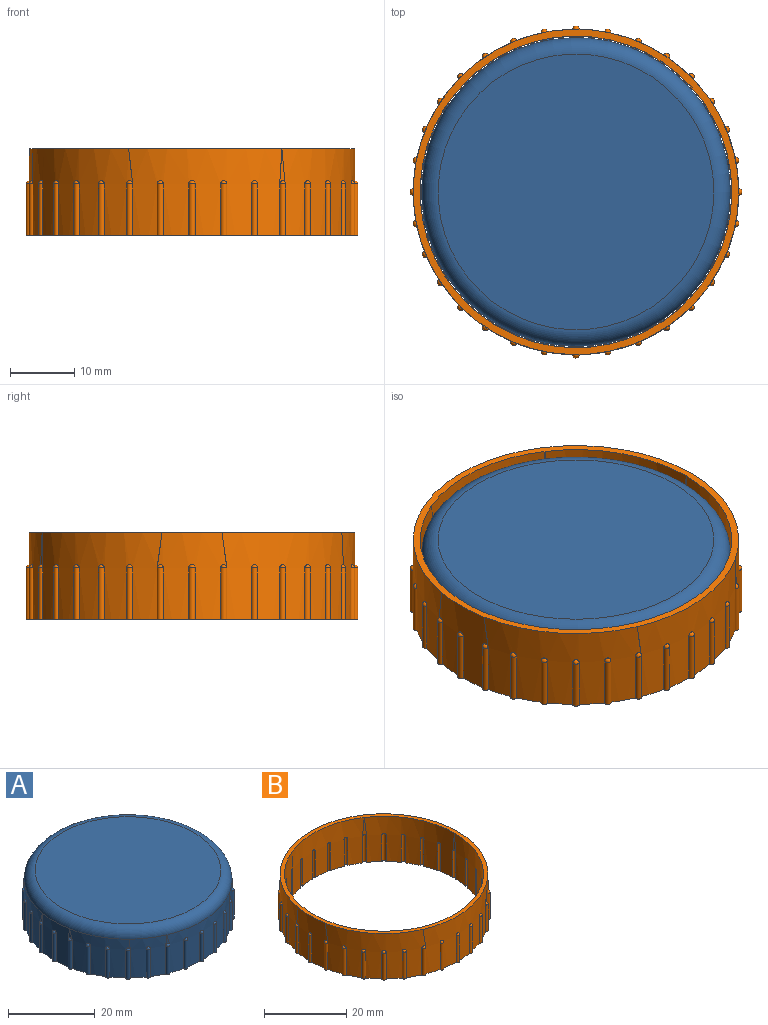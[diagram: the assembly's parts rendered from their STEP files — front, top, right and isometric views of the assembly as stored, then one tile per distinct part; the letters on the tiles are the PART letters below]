
ASSEMBLY  parts=2 mates=1
PART A: 68 faces, bbox 52x52x13.5 mm
  f0: cylinder r=24mm len=48mm, axis (0,0,-1), area 1388.7mm2, adj f2,f3,f4,f5,f6,f7,f8,f9
  f1: plane 42.92x42.92mm, normal (0,0,1), area 1446.8mm2, adj f3
  f2: plane 49x49mm, normal (0,0,-1), area 1822.2mm2, adj f0,f4,f5,f6,f7,f8,f9,f10
  f3: torus R=21.46mm, axis (0,0,1), area 578.5mm2, adj f0,f1
  f4: cylinder r=0.5mm len=8mm, axis (0,0,-1), area 12.6mm2, adj f0,f2,f67
  f5: cylinder r=0.5mm len=8mm, axis (0,0,-1), area 12.6mm2, adj f0,f2,f66
  f6: cylinder r=0.5mm len=8mm, axis (0,0,-1), area 12.6mm2, adj f0,f2,f65
  f7: cylinder r=0.5mm len=8mm, axis (0,0,-1), area 12.6mm2, adj f0,f2,f64
  f8: cylinder r=0.5mm len=8mm, axis (0,0,-1), area 12.6mm2, adj f0,f2,f63
  f9: cylinder r=0.5mm len=8mm, axis (0,0,-1), area 12.6mm2, adj f0,f2,f62
  f10: cylinder r=0.5mm len=8mm, axis (0,0,-1), area 12.6mm2, adj f0,f2,f61
  f11: cylinder r=0.5mm len=8mm, axis (0,0,-1), area 12.6mm2, adj f0,f2,f60
  f12: cylinder r=0.5mm len=8mm, axis (0,0,-1), area 12.6mm2, adj f0,f2,f59
  f13: cylinder r=0.5mm len=8mm, axis (0,0,-1), area 12.6mm2, adj f0,f2,f58
  f14: cylinder r=0.5mm len=8mm, axis (0,0,-1), area 12.6mm2, adj f0,f2,f57
  f15: cylinder r=0.5mm len=8mm, axis (0,0,-1), area 12.6mm2, adj f0,f2,f56
  f16: cylinder r=0.5mm len=8mm, axis (0,0,-1), area 12.6mm2, adj f0,f2,f55
  f17: cylinder r=0.5mm len=8mm, axis (0,0,-1), area 12.6mm2, adj f0,f2,f54
  f18: cylinder r=0.5mm len=8mm, axis (0,0,-1), area 12.6mm2, adj f0,f2,f53
  f19: cylinder r=0.5mm len=8mm, axis (0,0,-1), area 12.6mm2, adj f0,f2,f52
  f20: cylinder r=0.5mm len=8mm, axis (0,0,-1), area 12.6mm2, adj f0,f2,f51
  f21: cylinder r=0.5mm len=8mm, axis (0,0,-1), area 12.6mm2, adj f0,f2,f50
  f22: cylinder r=0.5mm len=8mm, axis (0,0,-1), area 12.6mm2, adj f0,f2,f49
  f23: cylinder r=0.5mm len=8mm, axis (0,0,-1), area 12.6mm2, adj f0,f2,f48
  f24: cylinder r=0.5mm len=8mm, axis (0,0,-1), area 12.6mm2, adj f0,f2,f47
  f25: cylinder r=0.5mm len=8mm, axis (0,0,-1), area 12.6mm2, adj f0,f2,f46
  f26: cylinder r=0.5mm len=8mm, axis (0,0,-1), area 12.6mm2, adj f0,f2,f45
  f27: cylinder r=0.5mm len=8mm, axis (0,0,-1), area 12.6mm2, adj f0,f2,f44
  f28: cylinder r=0.5mm len=8mm, axis (0,0,-1), area 12.6mm2, adj f0,f2,f43
  f29: cylinder r=0.5mm len=8mm, axis (0,0,-1), area 12.6mm2, adj f0,f2,f42
  f30: cylinder r=0.5mm len=8mm, axis (0,0,-1), area 12.6mm2, adj f0,f2,f41
  f31: cylinder r=0.5mm len=8mm, axis (0,0,-1), area 12.6mm2, adj f0,f2,f40
  f32: cylinder r=0.5mm len=8mm, axis (0,0,-1), area 12.6mm2, adj f0,f2,f39
  f33: cylinder r=0.5mm len=8mm, axis (0,0,-1), area 12.6mm2, adj f0,f2,f38
  f34: cylinder r=0.5mm len=8mm, axis (0,0,-1), area 12.6mm2, adj f0,f2,f37
  f35: cylinder r=0.5mm len=8mm, axis (0,0,-1), area 12.6mm2, adj f0,f2,f36
  f36: sphere r=0.5mm, area 0.8mm2, adj f0,f35
  f37: sphere r=0.5mm, area 0.8mm2, adj f0,f34
  f38: sphere r=0.5mm, area 0.7mm2, adj f0,f33
  f39: sphere r=0.5mm, area 0.7mm2, adj f0,f32
  f40: sphere r=0.5mm, area 0.7mm2, adj f0,f31
  f41: sphere r=0.5mm, area 0.5mm2, adj f0,f30
  f42: sphere r=0.5mm, area 0.5mm2, adj f0,f29
  f43: sphere r=0.5mm, area 0.8mm2, adj f0,f28
  f44: sphere r=0.5mm, area 0.7mm2, adj f0,f27
  f45: sphere r=0.5mm, area 0.7mm2, adj f0,f26
  f46: sphere r=0.5mm, area 0.7mm2, adj f0,f25
  f47: sphere r=0.5mm, area 0.7mm2, adj f0,f24
  f48: sphere r=0.5mm, area 0.7mm2, adj f0,f23
  f49: sphere r=0.5mm, area 0.8mm2, adj f0,f22
  f50: sphere r=0.5mm, area 0.8mm2, adj f0,f21
  f51: sphere r=0.5mm, area 0.8mm2, adj f0,f20
  f52: sphere r=0.5mm, area 0.8mm2, adj f0,f19
  f53: sphere r=0.5mm, area 0.8mm2, adj f0,f18
  f54: sphere r=0.5mm, area 0.8mm2, adj f0,f17
  f55: sphere r=0.5mm, area 0.8mm2, adj f0,f16
  f56: sphere r=0.5mm, area 0.8mm2, adj f0,f15
  f57: sphere r=0.5mm, area 0.8mm2, adj f0,f14
  f58: sphere r=0.5mm, area 0.8mm2, adj f0,f13
  f59: sphere r=0.5mm, area 0.8mm2, adj f0,f12
  f60: sphere r=0.5mm, area 0.8mm2, adj f0,f11
  f61: sphere r=0.5mm, area 0.8mm2, adj f0,f10
  f62: sphere r=0.5mm, area 0.8mm2, adj f0,f9
  f63: sphere r=0.5mm, area 0.8mm2, adj f0,f8
  f64: sphere r=0.5mm, area 0.8mm2, adj f0,f7
  f65: sphere r=0.5mm, area 0.8mm2, adj f0,f6
  f66: sphere r=0.5mm, area 0.8mm2, adj f0,f5
  f67: sphere r=0.5mm, area 0.8mm2, adj f0,f4
PART B: 132 faces, bbox 51.6x51.6x13.5 mm
  f0: cylinder r=0.5mm len=8mm, axis (0,0,-1), area 12.6mm2, adj f65,f66,f99
  f1: cylinder r=0.5mm len=8mm, axis (0,0,-1), area 12.6mm2, adj f65,f66,f98
  f2: cylinder r=0.5mm len=8mm, axis (0,0,-1), area 12.6mm2, adj f65,f66,f97
  f3: cylinder r=0.5mm len=8mm, axis (0,0,-1), area 12.6mm2, adj f65,f66,f96
  f4: cylinder r=0.5mm len=8mm, axis (0,0,-1), area 12.6mm2, adj f65,f66,f95
  f5: cylinder r=0.5mm len=8mm, axis (0,0,-1), area 12.6mm2, adj f65,f66,f94
  f6: cylinder r=0.5mm len=8mm, axis (0,0,-1), area 12.6mm2, adj f65,f66,f93
  f7: cylinder r=0.5mm len=8mm, axis (0,0,-1), area 12.6mm2, adj f65,f66,f92
  f8: cylinder r=0.5mm len=8mm, axis (0,0,-1), area 12.6mm2, adj f65,f66,f91
  f9: cylinder r=0.5mm len=8mm, axis (0,0,-1), area 12.6mm2, adj f65,f66,f90
  f10: cylinder r=0.5mm len=8mm, axis (0,0,-1), area 12.6mm2, adj f65,f66,f89
  f11: cylinder r=0.5mm len=8mm, axis (0,0,-1), area 12.6mm2, adj f65,f66,f88
  f12: cylinder r=0.5mm len=8mm, axis (0,0,-1), area 12.6mm2, adj f65,f66,f87
  f13: cylinder r=0.5mm len=8mm, axis (0,0,-1), area 12.6mm2, adj f65,f66,f86
  f14: cylinder r=0.5mm len=8mm, axis (0,0,-1), area 12.6mm2, adj f65,f66,f85
  f15: cylinder r=0.5mm len=8mm, axis (0,0,-1), area 12.6mm2, adj f65,f66,f84
  f16: cylinder r=0.5mm len=8mm, axis (0,0,-1), area 12.6mm2, adj f65,f66,f83
  f17: cylinder r=0.5mm len=8mm, axis (0,0,-1), area 12.6mm2, adj f65,f66,f82
  f18: cylinder r=0.5mm len=8mm, axis (0,0,-1), area 12.6mm2, adj f65,f66,f81
  f19: cylinder r=0.5mm len=8mm, axis (0,0,-1), area 12.6mm2, adj f65,f66,f80
  f20: cylinder r=0.5mm len=8mm, axis (0,0,-1), area 12.6mm2, adj f65,f66,f79
  f21: cylinder r=0.5mm len=8mm, axis (0,0,-1), area 12.6mm2, adj f65,f66,f78
  f22: cylinder r=0.5mm len=8mm, axis (0,0,-1), area 12.6mm2, adj f65,f66,f77
  f23: cylinder r=0.5mm len=8mm, axis (0,0,-1), area 12.6mm2, adj f65,f66,f76
  f24: cylinder r=0.5mm len=8mm, axis (0,0,-1), area 12.6mm2, adj f65,f66,f75
  f25: cylinder r=0.5mm len=8mm, axis (0,0,-1), area 12.6mm2, adj f65,f66,f74
  f26: cylinder r=0.5mm len=8mm, axis (0,0,-1), area 12.6mm2, adj f65,f66,f73
  f27: cylinder r=0.5mm len=8mm, axis (0,0,-1), area 12.6mm2, adj f65,f66,f72
  f28: cylinder r=0.5mm len=8mm, axis (0,0,-1), area 12.6mm2, adj f65,f66,f71
  f29: cylinder r=0.5mm len=8mm, axis (0,0,-1), area 12.6mm2, adj f65,f66,f70
  f30: cylinder r=0.5mm len=8mm, axis (0,0,-1), area 12.6mm2, adj f65,f66,f69
  f31: cylinder r=0.5mm len=8mm, axis (0,0,-1), area 12.6mm2, adj f65,f66,f68
  f32: cylinder r=0.5mm len=8mm, axis (0,0,-1), area 12.6mm2, adj f63,f66,f131
  f33: cylinder r=0.5mm len=8mm, axis (0,0,-1), area 12.6mm2, adj f63,f66,f130
  f34: cylinder r=0.5mm len=8mm, axis (0,0,-1), area 12.6mm2, adj f63,f66,f129
  f35: cylinder r=0.5mm len=8mm, axis (0,0,-1), area 12.6mm2, adj f63,f66,f128
  f36: cylinder r=0.5mm len=8mm, axis (0,0,-1), area 12.6mm2, adj f63,f66,f127
  f37: cylinder r=0.5mm len=8mm, axis (0,0,-1), area 12.6mm2, adj f63,f66,f126
  f38: cylinder r=0.5mm len=8mm, axis (0,0,-1), area 12.6mm2, adj f63,f66,f125
  f39: cylinder r=0.5mm len=8mm, axis (0,0,-1), area 12.6mm2, adj f63,f66,f124
  f40: cylinder r=0.5mm len=8mm, axis (0,0,-1), area 12.6mm2, adj f63,f66,f123
  f41: cylinder r=0.5mm len=8mm, axis (0,0,-1), area 12.6mm2, adj f63,f66,f122
  f42: cylinder r=0.5mm len=8mm, axis (0,0,-1), area 12.6mm2, adj f63,f66,f121
  f43: cylinder r=0.5mm len=8mm, axis (0,0,-1), area 12.6mm2, adj f63,f66,f120
  f44: cylinder r=0.5mm len=8mm, axis (0,0,-1), area 12.6mm2, adj f63,f66,f119
  f45: cylinder r=0.5mm len=8mm, axis (0,0,-1), area 12.6mm2, adj f63,f66,f118
  f46: cylinder r=0.5mm len=8mm, axis (0,0,-1), area 12.6mm2, adj f63,f66,f117
  f47: cylinder r=0.5mm len=8mm, axis (0,0,-1), area 12.6mm2, adj f63,f66,f116
  f48: cylinder r=0.5mm len=8mm, axis (0,0,-1), area 12.6mm2, adj f63,f66,f115
  f49: cylinder r=0.5mm len=8mm, axis (0,0,-1), area 12.6mm2, adj f63,f66,f114
  f50: cylinder r=0.5mm len=8mm, axis (0,0,-1), area 12.6mm2, adj f63,f66,f113
  f51: cylinder r=0.5mm len=8mm, axis (0,0,-1), area 12.6mm2, adj f63,f66,f112
  f52: cylinder r=0.5mm len=8mm, axis (0,0,-1), area 12.6mm2, adj f63,f66,f111
  f53: cylinder r=0.5mm len=8mm, axis (0,0,-1), area 12.6mm2, adj f63,f66,f110
  f54: cylinder r=0.5mm len=8mm, axis (0,0,-1), area 12.6mm2, adj f63,f66,f109
  f55: cylinder r=0.5mm len=8mm, axis (0,0,-1), area 12.6mm2, adj f63,f66,f108
  f56: cylinder r=0.5mm len=8mm, axis (0,0,-1), area 12.6mm2, adj f63,f66,f107
  f57: cylinder r=0.5mm len=8mm, axis (0,0,-1), area 12.6mm2, adj f63,f66,f106
  f58: cylinder r=0.5mm len=8mm, axis (0,0,-1), area 12.6mm2, adj f63,f66,f105
  f59: cylinder r=0.5mm len=8mm, axis (0,0,-1), area 12.6mm2, adj f63,f66,f104
  f60: cylinder r=0.5mm len=8mm, axis (0,0,-1), area 12.6mm2, adj f63,f66,f103
  f61: cylinder r=0.5mm len=8mm, axis (0,0,-1), area 12.6mm2, adj f63,f66,f102
  f62: cylinder r=0.5mm len=8mm, axis (0,0,-1), area 12.6mm2, adj f63,f66,f101
  f63: cylinder r=24.25mm len=48.5mm, axis (0,0,-1), area 1793mm2, adj f32,f33,f34,f35,f36,f37,f38,f39
  f64: cylinder r=0.5mm len=8mm, axis (0,0,-1), area 12.6mm2, adj f63,f66,f100
  f65: cylinder r=25.32mm len=50.65mm, axis (0,0,-1), area 1884.1mm2, adj f0,f1,f2,f3,f4,f5,f6,f7
  f66: plane 51.65x51.65mm, normal (0,0,-1), area 167.4mm2, adj f0,f1,f2,f3,f4,f5,f6,f7
  f67: plane 50.65x50.65mm, normal (0,0,1), area 167.4mm2, adj f63,f65
  f68: sphere r=0.5mm, area 0.6mm2, adj f31,f65
  f69: sphere r=0.5mm, area 0.6mm2, adj f30,f65
  f70: sphere r=0.5mm, area 0.8mm2, adj f29,f65
  f71: sphere r=0.5mm, area 0.8mm2, adj f28,f65
  f72: sphere r=0.5mm, area 0.8mm2, adj f27,f65
  f73: sphere r=0.5mm, area 0.8mm2, adj f26,f65
  f74: sphere r=0.5mm, area 0.8mm2, adj f25,f65
  f75: sphere r=0.5mm, area 0.8mm2, adj f24,f65
  f76: sphere r=0.5mm, area 0.8mm2, adj f23,f65
  f77: sphere r=0.5mm, area 0.8mm2, adj f22,f65
  f78: sphere r=0.5mm, area 0.8mm2, adj f21,f65
  f79: sphere r=0.5mm, area 0.8mm2, adj f20,f65
  f80: sphere r=0.5mm, area 0.8mm2, adj f19,f65
  f81: sphere r=0.5mm, area 0.8mm2, adj f18,f65
  f82: sphere r=0.5mm, area 0.8mm2, adj f17,f65
  f83: sphere r=0.5mm, area 0.8mm2, adj f16,f65
  f84: sphere r=0.5mm, area 0.8mm2, adj f15,f65
  f85: sphere r=0.5mm, area 0.8mm2, adj f14,f65
  f86: sphere r=0.5mm, area 0.8mm2, adj f13,f65
  f87: sphere r=0.5mm, area 0.8mm2, adj f12,f65
  f88: sphere r=0.5mm, area 0.8mm2, adj f11,f65
  f89: sphere r=0.5mm, area 0.8mm2, adj f10,f65
  f90: sphere r=0.5mm, area 0.8mm2, adj f9,f65
  f91: sphere r=0.5mm, area 0.8mm2, adj f8,f65
  f92: sphere r=0.5mm, area 0.8mm2, adj f7,f65
  f93: sphere r=0.5mm, area 0.8mm2, adj f6,f65
  f94: sphere r=0.5mm, area 0.8mm2, adj f5,f65
  f95: sphere r=0.5mm, area 0.8mm2, adj f4,f65
  f96: sphere r=0.5mm, area 0.8mm2, adj f3,f65
  f97: sphere r=0.5mm, area 0.8mm2, adj f2,f65
  f98: sphere r=0.5mm, area 0.8mm2, adj f1,f65
  f99: sphere r=0.5mm, area 0.8mm2, adj f0,f65
  f100: sphere r=0.5mm, area 0.8mm2, adj f63,f64
  f101: sphere r=0.5mm, area 0.8mm2, adj f62,f63
  f102: sphere r=0.5mm, area 0.8mm2, adj f61,f63
  f103: sphere r=0.5mm, area 0.8mm2, adj f60,f63
  f104: sphere r=0.5mm, area 0.8mm2, adj f59,f63
  f105: sphere r=0.5mm, area 0.8mm2, adj f58,f63
  f106: sphere r=0.5mm, area 0.8mm2, adj f57,f63
  f107: sphere r=0.5mm, area 0.8mm2, adj f56,f63
  f108: sphere r=0.5mm, area 0.8mm2, adj f55,f63
  f109: sphere r=0.5mm, area 0.8mm2, adj f54,f63
  f110: sphere r=0.5mm, area 0.8mm2, adj f53,f63
  f111: sphere r=0.5mm, area 0.8mm2, adj f52,f63
  f112: sphere r=0.5mm, area 0.8mm2, adj f51,f63
  f113: sphere r=0.5mm, area 0.8mm2, adj f50,f63
  f114: sphere r=0.5mm, area 0.8mm2, adj f49,f63
  f115: sphere r=0.5mm, area 0.8mm2, adj f48,f63
  f116: sphere r=0.5mm, area 0.8mm2, adj f47,f63
  f117: sphere r=0.5mm, area 0.8mm2, adj f46,f63
  f118: sphere r=0.5mm, area 0.8mm2, adj f45,f63
  f119: sphere r=0.5mm, area 0.8mm2, adj f44,f63
  f120: sphere r=0.5mm, area 0.8mm2, adj f43,f63
  f121: sphere r=0.5mm, area 0.8mm2, adj f42,f63
  f122: sphere r=0.5mm, area 0.8mm2, adj f41,f63
  f123: sphere r=0.5mm, area 0.8mm2, adj f40,f63
  f124: sphere r=0.5mm, area 0.8mm2, adj f39,f63
  f125: sphere r=0.5mm, area 0.8mm2, adj f38,f63
  f126: sphere r=0.5mm, area 0.8mm2, adj f37,f63
  f127: sphere r=0.5mm, area 0.8mm2, adj f36,f63
  f128: sphere r=0.5mm, area 0.8mm2, adj f35,f63
  f129: sphere r=0.5mm, area 0.8mm2, adj f34,f63
  f130: sphere r=0.5mm, area 0.8mm2, adj f33,f63
  f131: sphere r=0.5mm, area 0.8mm2, adj f32,f63
PLACE A t=(32.19,25.44,3.54)mm
PLACE B t=(32.19,25.44,3.54)mm
MATE planar A.f0 <-> B.f63  axis (0,0,-1) through (32.19,25.44,3.54)mm
